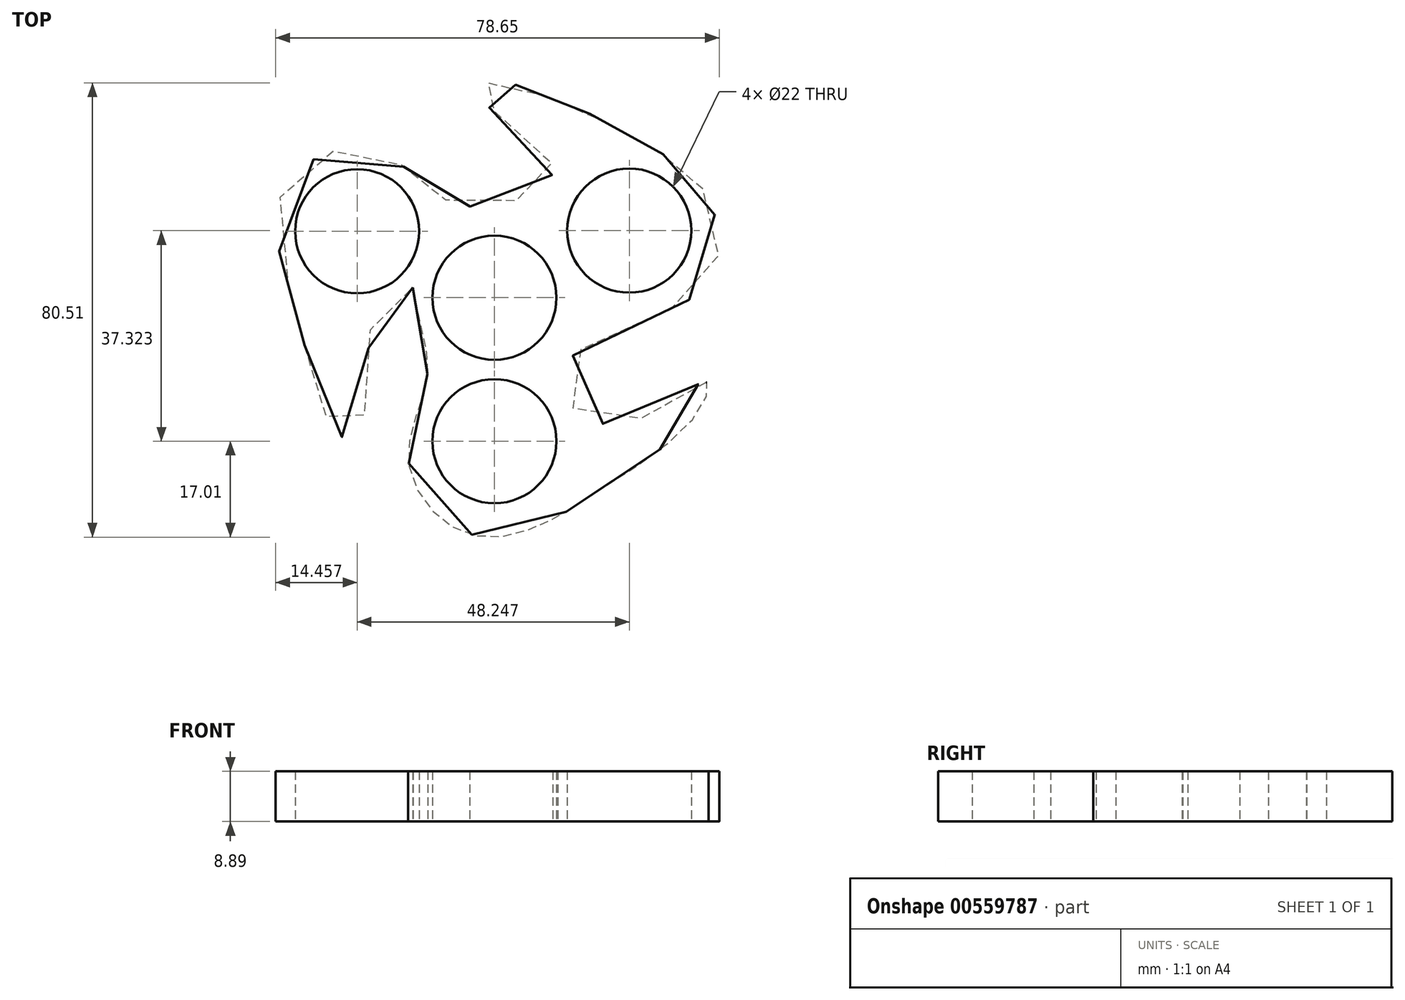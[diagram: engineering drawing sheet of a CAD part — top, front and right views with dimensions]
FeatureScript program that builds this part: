
annotation { "Feature Type Name" : "Feature", "Feature Type Description" : "" }
export const myFeature = defineFeature(function(context is Context, id is Id, definition is map)
    precondition{}
    {
        {
            var Q0;
            Q0=qCreatedBy(makeId("Top.planeOp"),FACE);
            var sketch = newSketch(context, id + "F0", { "sketchPlane" : qUnion([Q0])});
            skCircle(sketch, "E0", {"center": v(0, 25.43) * mm, "radius": 11 * mm});
            skCircle(sketch, "E1", {"center": v(0, 0) * mm, "radius": 11 * mm});
            skCircle(sketch, "E2", {"center": v(-24.33, 37.21) * mm, "radius": 11 * mm});
            skCircle(sketch, "E3", {"center": v(23.91, 37.32) * mm, "radius": 11 * mm});
            skFitSpline(sketch, "E4", {"points": [v(-14.47, 27.22) * mm, v(-14.47, 26.91) * mm, v(-12.04, 15.7) * mm, v(-12.76, 7.82) * mm, v(-15.27, -2.95) * mm, v(-10, -13.27) * mm, v(0, -17) * mm, v(11.32, -13.27) * mm, v(18.77, -8.53) * mm, v(35.55, 4.37) * mm, v(37.57, 10.42) * mm, v(27.84, 4.96) * mm, v(17.41, 3.65) * mm, v(11.25, 11.1) * mm, v(24.13, 20.78) * mm, v(37.7, 27.67) * mm, v(39.6, 37.79) * mm, v(35.93, 46.09) * mm, v(30.48, 50.54) * mm, v(24.12, 54.01) * mm, v(16.17, 58.36) * mm, v(8.26, 61.44) * mm, v(2.57, 63.38) * mm, v(-4.3, 62.44) * mm, v(0, 58.5) * mm, v(9.96, 49.7) * mm, v(9.33, 45.82) * mm, v(0, 41.7) * mm, v(-9.38, 43.09) * mm, v(-13.87, 46.96) * mm, v(-22.77, 51.57) * mm, v(-32.73, 49.55) * mm, v(-38.72, 40.19) * mm, v(-35.4, 24.3) * mm, v(-33.7, 17.2) * mm, v(-31.67, 8.05) * mm, v(-24.9, 0) * mm, v(-22.3, 16.27) * mm, v(-20.84, 21.6) * mm, v(-14.47, 27.22) * mm]});
            skFitSpline(sketch, "E5", {"points": [v(145.1, -39.24) * mm, v(140.6, -35.37) * mm], "startDerivative": vector(-4.5, 3.87) * mm, "endDerivative": vector(-4.5, 3.87) * mm});
            skSolve(sketch);
        }
        {
            var Q0;
            Q0 = qSketchRegion(id + "F0", true);
            extrude(context, id + "F1", {"entities" : qUnion([Q0]), "depth" : 8.9 * mm, "offsetDistance" : 25.4 * mm});
        }
    });
